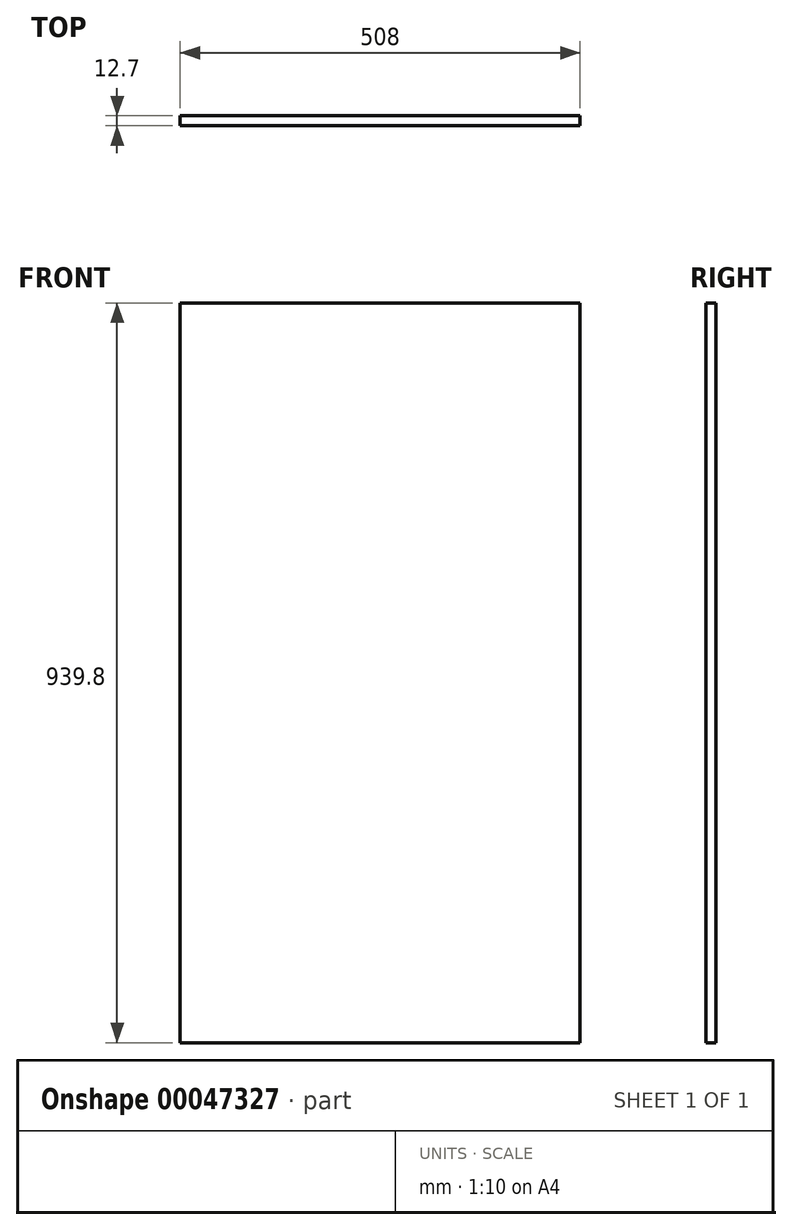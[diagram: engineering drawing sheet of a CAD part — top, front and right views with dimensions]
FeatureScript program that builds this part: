
annotation { "Feature Type Name" : "Feature", "Feature Type Description" : "" }
export const myFeature = defineFeature(function(context is Context, id is Id, definition is map)
    precondition{}
    {
        {
            var Q0;
            Q0=qCreatedBy(makeId("Front.planeOp"),FACE);
            var sketch = newSketch(context, id + "F0", { "sketchPlane" : qUnion([Q0])});
            skLineSegment(sketch, "E0.bottom", {"start": v(-27.14, 887.12) * mm, "end": v(480.86, 887.12) * mm});
            skLineSegment(sketch, "E0.top", {"start": v(-27.14, -52.68) * mm, "end": v(480.86, -52.68) * mm});
            skLineSegment(sketch, "E0.left", {"start": v(-27.14, 887.12) * mm, "end": v(-27.14, -52.68) * mm});
            skLineSegment(sketch, "E0.right", {"start": v(480.86, 887.12) * mm, "end": v(480.86, -52.68) * mm});
            skSolve(sketch);
        }
        {
            var Q0;
            Q0=makeQuery(id+"F0.imprint","IMPRINT",FACE,{"disambiguationData":[TD([[makeQuery(id+"F0.imprint","IMPRINT",EDGE,{"derivedFrom":sQuery(id+"F0.wireOp",EDGE,"E0.bottom")}),-1.0]])]});
            extrude(context, id + "F1", {"entities" : qUnion([Q0]), "depth" : 12.7 * mm});
        }
    });
